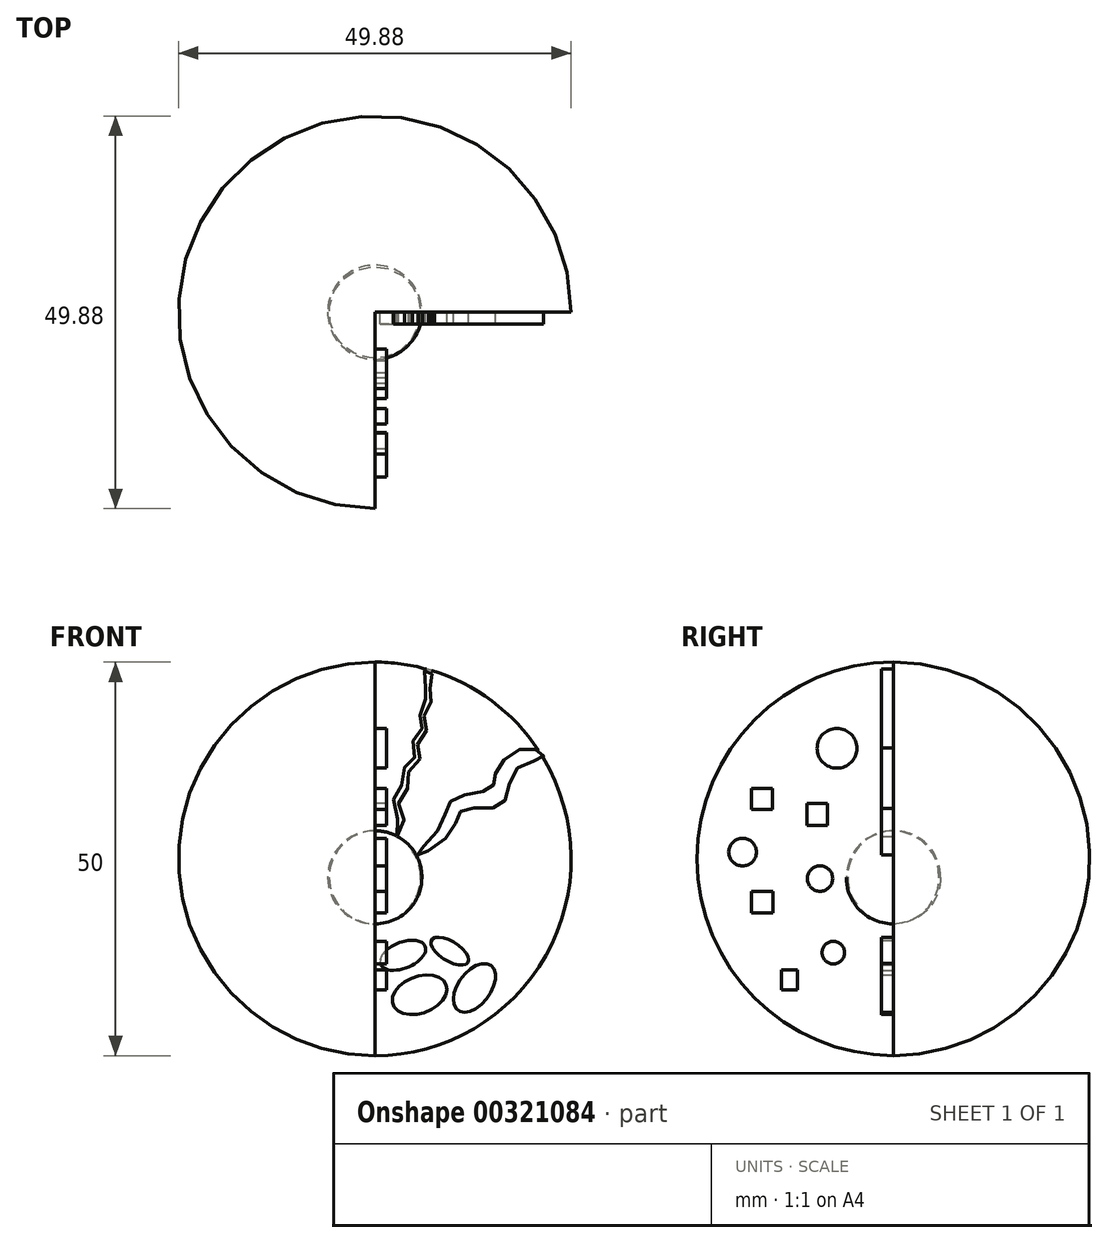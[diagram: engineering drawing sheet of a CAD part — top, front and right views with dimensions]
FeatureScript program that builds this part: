
annotation { "Feature Type Name" : "Feature", "Feature Type Description" : "" }
export const myFeature = defineFeature(function(context is Context, id is Id, definition is map)
    precondition{}
    {
        {
            var Q0;
            Q0=qCreatedBy(makeId("Front.planeOp"),FACE);
            var sketch = newSketch(context, id + "F0", { "sketchPlane" : qUnion([Q0])});
            skLineSegment(sketch, "E0", {"start": v(0, 0) * mm, "end": v(0, 50) * mm});
            skArc(sketch, "E1", {"start": v(0, 0) * mm, "mid": v(24.94, 25) * mm, "end": v(0, 50) * mm});
            skSolve(sketch);
        }
        {
            var Q0;
            Q0 = qSketchRegion(id + "F0", true);
            var Q1;
            Q1=sQuery(id+"F0.wireOp",EDGE,"E0");
            revolve(context, id + "F1", {"entities" : qUnion([Q0]), "axis" : qUnion([Q1]), "revolveType" : RevolveType.ONE_DIRECTION, "angle" : 270 * degree});
        }
        {
            var Q0;
            Q0=qCreatedBy(makeId("Right.planeOp"),FACE);
            var sketch = newSketch(context, id + "F2", { "sketchPlane" : qUnion([Q0])});
            skLineSegment(sketch, "E2", {"start": v(0, 16.76) * mm, "end": v(0, 28.56) * mm});
            skArc(sketch, "E3", {"start": v(0, 16.76) * mm, "mid": v(5.98, 22.66) * mm, "end": v(0, 28.56) * mm});
            skSolve(sketch);
        }
        {
            var Q0;
            Q0 = qSketchRegion(id + "F2", true);
            var Q1;
            Q1=sQuery(id+"F0.wireOp",EDGE,"E0");
            revolve(context, id + "F3", {"entities" : qUnion([Q0]), "axis" : qUnion([Q1]), "revolveType" : RevolveType.FULL});
        }
        {
            var Q0;
            Q0=makeQuery(id+"F0.imprint","IMPRINT",FACE,{"disambiguationData":[TD([[makeQuery(id+"F0.imprint","IMPRINT",EDGE,{"derivedFrom":sQuery(id+"F0.wireOp",EDGE,"E0")}),-1.0]])]});
            var sketch = newSketch(context, id + "F4", { "sketchPlane" : qUnion([Q0])});
            skFitSpline(sketch, "E4", {"points": [v(2.8, 27.85) * mm, v(3.7, 30.3) * mm, v(3.03, 32.25) * mm, v(4.4, 34.4) * mm, v(4.39, 36.43) * mm, v(5.97, 38.09) * mm, v(5.38, 40.03) * mm, v(6.88, 41.88) * mm, v(6.1, 43.7) * mm, v(7.6, 45.56) * mm, v(6.81, 47.16) * mm, v(7.28, 48.73) * mm, v(6.53, 49.1) * mm, v(6.2, 47.07) * mm, v(6.89, 45.93) * mm, v(5.54, 44) * mm, v(6.37, 41.91) * mm, v(4.85, 40.75) * mm, v(5.3, 38.2) * mm, v(3.94, 37.19) * mm, v(3.7, 34.93) * mm, v(2.42, 33) * mm, v(2.88, 30.4) * mm, v(2.8, 27.85) * mm]});
            skSolve(sketch);
        }
        {
            var Q0;
            Q0 = qSketchRegion(id + "F4", true);
            extrude(context, id + "F5", {"entities" : qUnion([Q0]), "depth" : 1.5 * mm});
        }
        {
            var Q0;
            Q0=makeQuery(id+"F0.imprint","IMPRINT",FACE,{"disambiguationData":[TD([[makeQuery(id+"F0.imprint","IMPRINT",EDGE,{"derivedFrom":sQuery(id+"F0.wireOp",EDGE,"E0")}),-1.0]])]});
            var sketch = newSketch(context, id + "F6", { "sketchPlane" : qUnion([Q0])});
            skFitSpline(sketch, "E5", {"points": [v(5.4, 25.5) * mm, v(9.56, 28.18) * mm, v(11.22, 31.28) * mm, v(16.07, 31.83) * mm, v(17.9, 36.33) * mm, v(21.44, 38) * mm, v(19.46, 39.09) * mm, v(15.46, 36.21) * mm, v(14.75, 33.98) * mm, v(10, 32.62) * mm, v(8.26, 29) * mm, v(5.4, 25.5) * mm]});
            skSolve(sketch);
        }
        {
            var Q0;
            Q0 = qSketchRegion(id + "F6", true);
            extrude(context, id + "F7", {"entities" : qUnion([Q0]), "depth" : 1.5 * mm});
        }
        {
            var Q0;
            Q0=makeQuery(id+"F0.imprint","IMPRINT",FACE,{"disambiguationData":[TD([[makeQuery(id+"F0.imprint","IMPRINT",EDGE,{"derivedFrom":sQuery(id+"F0.wireOp",EDGE,"E0")}),-1.0]])]});
            var sketch = newSketch(context, id + "F8", { "sketchPlane" : qUnion([Q0])});
            skEllipse(sketch, "E6", {"center": v(5.7, 7.74) * mm, "majorRadius": 3.6 * mm, "minorRadius": 2.34 * mm, "majorAxis": v(0.94, 0.35)});
            skSolve(sketch);
        }
        {
            var Q0;
            Q0 = qSketchRegion(id + "F8", true);
            extrude(context, id + "F9", {"entities" : qUnion([Q0]), "depth" : 1.5 * mm});
        }
        {
            var Q0;
            Q0=makeQuery(id+"F0.imprint","IMPRINT",FACE,{"disambiguationData":[TD([[makeQuery(id+"F0.imprint","IMPRINT",EDGE,{"derivedFrom":sQuery(id+"F0.wireOp",EDGE,"E0")}),-1.0]])]});
            var sketch = newSketch(context, id + "F10", { "sketchPlane" : qUnion([Q0])});
            skEllipse(sketch, "E7", {"center": v(12.66, 8.62) * mm, "majorRadius": 3.53 * mm, "minorRadius": 2.07 * mm, "majorAxis": v(0.6, 0.8)});
            skSolve(sketch);
        }
        {
            var Q0;
            Q0 = qSketchRegion(id + "F10", true);
            extrude(context, id + "F11", {"entities" : qUnion([Q0]), "depth" : 1.5 * mm});
        }
        {
            var Q0;
            Q0=makeQuery(id+"F0.imprint","IMPRINT",FACE,{"disambiguationData":[TD([[makeQuery(id+"F0.imprint","IMPRINT",EDGE,{"derivedFrom":sQuery(id+"F0.wireOp",EDGE,"E0")}),-1.0]])]});
            var sketch = newSketch(context, id + "F12", { "sketchPlane" : qUnion([Q0])});
            skEllipse(sketch, "E8", {"center": v(3.57, 12.75) * mm, "majorRadius": 3.06 * mm, "minorRadius": 1.65 * mm, "majorAxis": v(0.93, 0.37)});
            skSolve(sketch);
        }
        {
            var Q0;
            Q0 = qSketchRegion(id + "F12", true);
            extrude(context, id + "F13", {"entities" : qUnion([Q0]), "depth" : 1.5 * mm});
        }
        {
            var Q0;
            Q0=makeQuery(id+"F0.imprint","IMPRINT",FACE,{"disambiguationData":[TD([[makeQuery(id+"F0.imprint","IMPRINT",EDGE,{"derivedFrom":sQuery(id+"F0.wireOp",EDGE,"E0")}),-1.0]])]});
            var sketch = newSketch(context, id + "F14", { "sketchPlane" : qUnion([Q0])});
            skEllipse(sketch, "E9", {"center": v(9.53, 13.27) * mm, "majorRadius": 2.7 * mm, "minorRadius": 1.24 * mm, "majorAxis": v(0.85, -0.52)});
            skSolve(sketch);
        }
        {
            var Q0;
            Q0 = qSketchRegion(id + "F14", true);
            extrude(context, id + "F15", {"entities" : qUnion([Q0]), "depth" : 1.5 * mm});
        }
        {
            var Q0;
            Q0=makeQuery(id+"F1.opRevolve","CAP_FACE",FACE,{"disambiguationData":[OSD([sQuery(id+"F0.wireOp",EDGE,"E0"),sQuery(id+"F0.wireOp",EDGE,"E1")])],"isStart":false});
            var sketch = newSketch(context, id + "F16", { "sketchPlane" : qUnion([Q0])});
            skLineSegment(sketch, "E10.bottom", {"start": v(-14.23, 8.35) * mm, "end": v(-12.2, 8.35) * mm});
            skLineSegment(sketch, "E10.top", {"start": v(-14.23, 10.92) * mm, "end": v(-12.2, 10.92) * mm});
            skLineSegment(sketch, "E10.left", {"start": v(-14.23, 8.35) * mm, "end": v(-14.23, 10.92) * mm});
            skLineSegment(sketch, "E10.right", {"start": v(-12.2, 8.35) * mm, "end": v(-12.2, 10.92) * mm});
            skSolve(sketch);
        }
        {
            var Q0;
            Q0 = qSketchRegion(id + "F16", true);
            extrude(context, id + "F17", {"entities" : qUnion([Q0]), "depth" : 1.5 * mm});
        }
        {
            var Q0;
            Q0=makeQuery(id+"F1.opRevolve","CAP_FACE",FACE,{"disambiguationData":[OSD([sQuery(id+"F0.wireOp",EDGE,"E0"),sQuery(id+"F0.wireOp",EDGE,"E1")])],"isStart":false});
            var sketch = newSketch(context, id + "F18", { "sketchPlane" : qUnion([Q0])});
            skLineSegment(sketch, "E11.bottom", {"start": v(-18.01, 18.16) * mm, "end": v(-15.3, 18.16) * mm});
            skLineSegment(sketch, "E11.top", {"start": v(-18.01, 20.9) * mm, "end": v(-15.3, 20.9) * mm});
            skLineSegment(sketch, "E11.left", {"start": v(-18.01, 18.16) * mm, "end": v(-18.01, 20.9) * mm});
            skLineSegment(sketch, "E11.right", {"start": v(-15.3, 18.16) * mm, "end": v(-15.3, 20.9) * mm});
            skSolve(sketch);
        }
        {
            var Q0;
            Q0 = qSketchRegion(id + "F18", true);
            extrude(context, id + "F19", {"entities" : qUnion([Q0]), "depth" : 1.5 * mm});
        }
        {
            var Q0;
            Q0=makeQuery(id+"F1.opRevolve","CAP_FACE",FACE,{"disambiguationData":[OSD([sQuery(id+"F0.wireOp",EDGE,"E0"),sQuery(id+"F0.wireOp",EDGE,"E1")])],"isStart":false});
            var sketch = newSketch(context, id + "F20", { "sketchPlane" : qUnion([Q0])});
            skLineSegment(sketch, "E12.bottom", {"start": v(-11, 29.23) * mm, "end": v(-8.38, 29.23) * mm});
            skLineSegment(sketch, "E12.top", {"start": v(-11, 32.05) * mm, "end": v(-8.38, 32.05) * mm});
            skLineSegment(sketch, "E12.left", {"start": v(-11, 29.23) * mm, "end": v(-11, 32.05) * mm});
            skLineSegment(sketch, "E12.right", {"start": v(-8.38, 29.23) * mm, "end": v(-8.38, 32.05) * mm});
            skSolve(sketch);
        }
        {
            var Q0;
            Q0 = qSketchRegion(id + "F20", true);
            extrude(context, id + "F21", {"entities" : qUnion([Q0]), "depth" : 1.5 * mm});
        }
        {
            var Q0;
            Q0=makeQuery(id+"F1.opRevolve","CAP_FACE",FACE,{"disambiguationData":[OSD([sQuery(id+"F0.wireOp",EDGE,"E0"),sQuery(id+"F0.wireOp",EDGE,"E1")])],"isStart":false});
            var sketch = newSketch(context, id + "F22", { "sketchPlane" : qUnion([Q0])});
            skLineSegment(sketch, "E13.bottom", {"start": v(-18.03, 31.3) * mm, "end": v(-15.37, 31.3) * mm});
            skLineSegment(sketch, "E13.top", {"start": v(-18.03, 33.95) * mm, "end": v(-15.37, 33.95) * mm});
            skLineSegment(sketch, "E13.left", {"start": v(-18.03, 31.3) * mm, "end": v(-18.03, 33.95) * mm});
            skLineSegment(sketch, "E13.right", {"start": v(-15.37, 31.3) * mm, "end": v(-15.37, 33.95) * mm});
            skSolve(sketch);
        }
        {
            var Q0;
            Q0 = qSketchRegion(id + "F22", true);
            extrude(context, id + "F23", {"entities" : qUnion([Q0]), "depth" : 1.5 * mm});
        }
        {
            var Q0;
            Q0=makeQuery(id+"F1.opRevolve","CAP_FACE",FACE,{"disambiguationData":[OSD([sQuery(id+"F0.wireOp",EDGE,"E0"),sQuery(id+"F0.wireOp",EDGE,"E1")])],"isStart":false});
            var sketch = newSketch(context, id + "F24", { "sketchPlane" : qUnion([Q0])});
            skCircle(sketch, "E14", {"center": v(-7.64, 13.1) * mm, "radius": 1.44 * mm});
            skSolve(sketch);
        }
        {
            var Q0;
            Q0=makeQuery(id+"F24.imprint","IMPRINT",FACE,{"disambiguationData":[TD([[makeQuery(id+"F24.imprint","IMPRINT",EDGE,{"derivedFrom":sQuery(id+"F24.wireOp",EDGE,"E14")}),1.0]])]});
            extrude(context, id + "F25", {"entities" : qUnion([Q0]), "depth" : 1.5 * mm});
        }
        {
            var Q0;
            Q0=makeQuery(id+"F1.opRevolve","CAP_FACE",FACE,{"disambiguationData":[OSD([sQuery(id+"F0.wireOp",EDGE,"E0"),sQuery(id+"F0.wireOp",EDGE,"E1")])],"isStart":false});
            var sketch = newSketch(context, id + "F26", { "sketchPlane" : qUnion([Q0])});
            skCircle(sketch, "E15", {"center": v(-9.32, 22.5) * mm, "radius": 1.62 * mm});
            skSolve(sketch);
        }
        {
            var Q0;
            Q0 = qSketchRegion(id + "F26", true);
            extrude(context, id + "F27", {"entities" : qUnion([Q0]), "depth" : 1.5 * mm});
        }
        {
            var Q0;
            Q0=makeQuery(id+"F1.opRevolve","CAP_FACE",FACE,{"disambiguationData":[OSD([sQuery(id+"F0.wireOp",EDGE,"E0"),sQuery(id+"F0.wireOp",EDGE,"E1")])],"isStart":false});
            var sketch = newSketch(context, id + "F28", { "sketchPlane" : qUnion([Q0])});
            skCircle(sketch, "E16", {"center": v(-7.17, 39.05) * mm, "radius": 2.52 * mm});
            skSolve(sketch);
        }
        {
            var Q0;
            Q0 = qSketchRegion(id + "F28", true);
            extrude(context, id + "F29", {"entities" : qUnion([Q0]), "depth" : 1.5 * mm});
        }
        {
            var Q0;
            Q0=makeQuery(id+"F1.opRevolve","CAP_FACE",FACE,{"disambiguationData":[OSD([sQuery(id+"F0.wireOp",EDGE,"E0"),sQuery(id+"F0.wireOp",EDGE,"E1")])],"isStart":false});
            var sketch = newSketch(context, id + "F30", { "sketchPlane" : qUnion([Q0])});
            skCircle(sketch, "E17", {"center": v(-19.17, 25.86) * mm, "radius": 1.76 * mm});
            skSolve(sketch);
        }
        {
            var Q0;
            Q0 = qSketchRegion(id + "F30", true);
            extrude(context, id + "F31", {"entities" : qUnion([Q0]), "depth" : 1.5 * mm});
        }
    });
